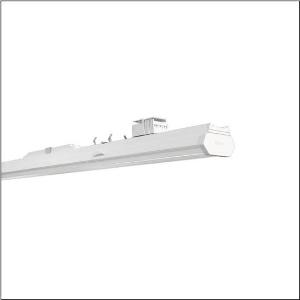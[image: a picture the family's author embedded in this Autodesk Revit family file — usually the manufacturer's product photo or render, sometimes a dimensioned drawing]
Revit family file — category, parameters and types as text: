
# Revit family: licross_r__11_protected_mo_51td127n485g_dbd9
name_source: partatom
category: Lighting Fixtures
units: mm (PartAtom-declared; Revit-internal decimal feet)

## family parameters
Cut with Voids When Loaded = No
Host = Face
Light Source = No
Part Type = Normal
Room Calculation Point = No
Round Connector Dimension = Use Diameter
Shared = No

## types (1)
- Licross® 11 Protected MO (1 x LED, 8720 lm, 48.6 W, 4000K)
    Apparent Load = 49 VA
    CIE Flux Codes = 73 92 98 99 100
    Color Rendering = 80
    Color Temperature = 4000K
    Default Elevation = 1800 mm
    Description = Licross® 11 Protected MO, luminaire insert, of sheet steel, galvanised, coil coated, white, length: 1.500mm, width: 90mm, height: 101mm, LED rated luminous flux: 8.720lm, light colour: 840, control gear: ON/OFF, with plug, 3-pole, with phase selection, mains connection: 220..240V, AC, 50/60Hz, rated input power: 49W, halogen-free wiring, primary light control with lens, of plastic, primary optical cover: cover, of PMMA, light emission: direct distribution, primary light characteristic: symmetric, protection rating (complete): IP54, insulation class (complete): insulation class I (protective earthing), certification: CE, ENEC, VDE, UKCA, protection symbol: D if used in an environment with non-conductive dust loads with corresponding accessories, impact resistance: IK06, permissible ambient temperature for indoor applications: -25..+35°C, corresponds to IFS (International Featured Standards) requirements for safety and quality in the food industry, reducing of maximum allowable ambient temperature of 5°C with ceiling mounting, LABS conformity tested according to VDMA 24364:2018-05, packaging unit: 1 piece
    Height = 92 mm
    Lamp = 1 x LED
    Lamp Light Flux = 8720 lm
    Lamp Power = 48.6 W
    Lamp count = 1
    Length = 1500 mm
    Luminous efficacy = 179 lm/W
    Manufacturer = Siteco
    ModVariant = No
    Model = 51TD127N485G
    Mounting Place = Ceiling
    Mounting Type = Pendant
    Number of Poles = 1
    OnlyDefault = Yes
    Power Factor = 1
    Product Name = Licross® 11 Protected MO
    Product group = luminaire insert
    ProductGroupID = 901
    Protection Class = Protection class I
    Protection Degree = IP 54
    RLX_Detail_Level = 1
    RLX_Emergency_Light_Flux = 0 lm
    RLX_Emergency_Type = 0
    RLX_Emergency_Type_DB = No
    RlxData = <blob elided: 20745 chars, md5=4baccac5>
    Socket = socket
    Standby Power = 0 W
    System Light Flux = 8720 lm
    System Power = 49 W
    Type Comments = Product without accessories
    Type Image = l_1256145.jpg
    URL = http://relux.com
    VarID = ---
    Voltage = 0 V
    Weight = 0.00 kg
    Width = 88 mm

## geometry (parser evidence)
native form markers: Blend x4, Sweep x10
no freeform markers — native parametric forms only
